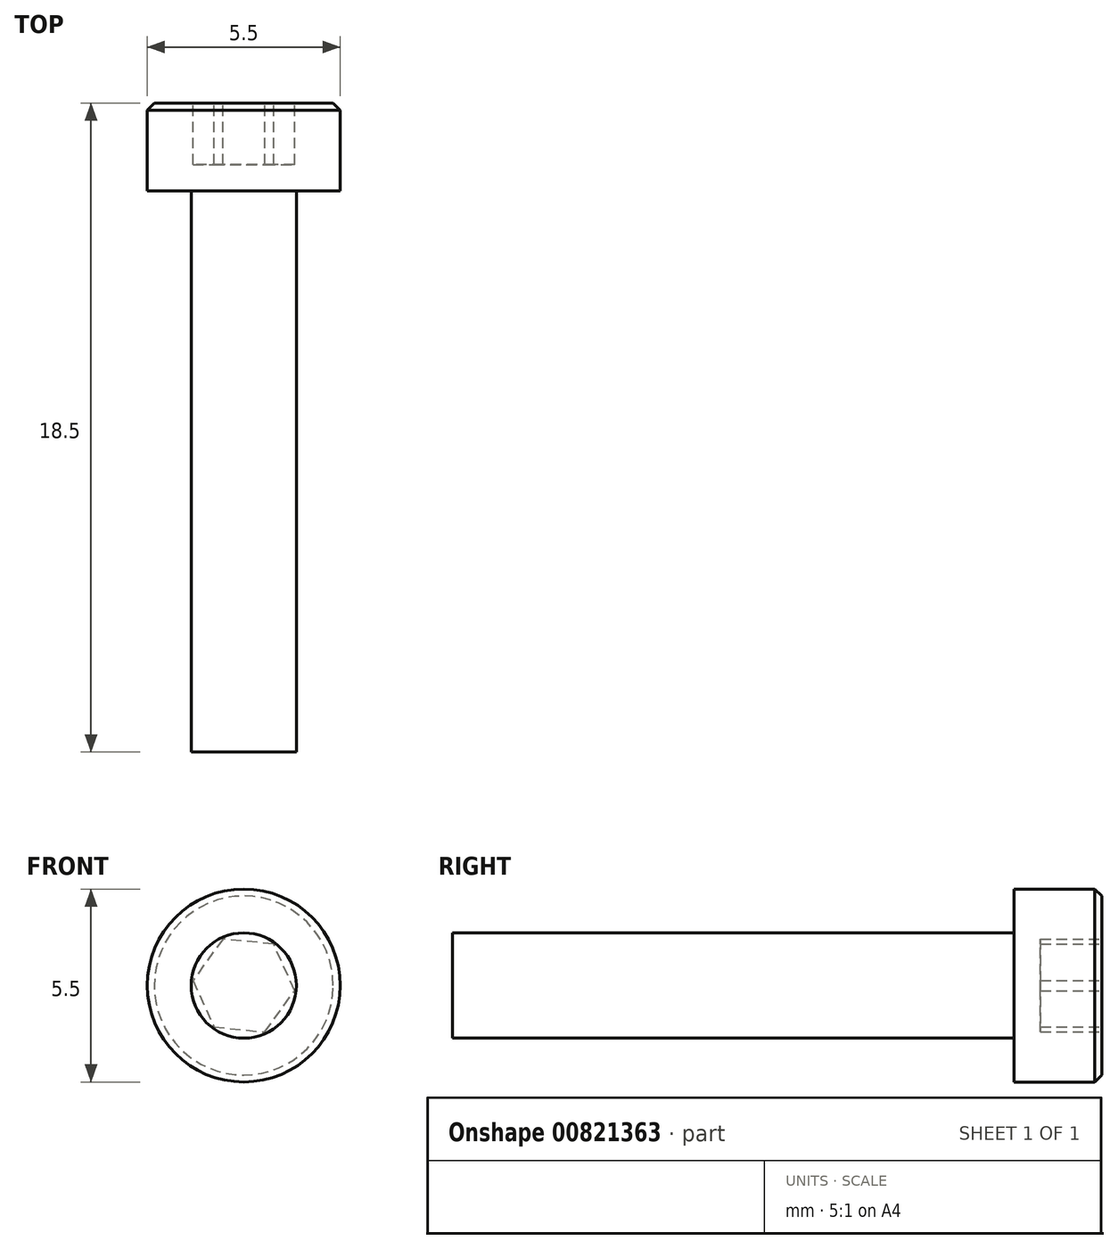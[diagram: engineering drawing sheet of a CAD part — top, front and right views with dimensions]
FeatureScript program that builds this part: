
annotation { "Feature Type Name" : "Feature", "Feature Type Description" : "" }
export const myFeature = defineFeature(function(context is Context, id is Id, definition is map)
    precondition{}
    {
        {
            var Q0;
            Q0=qCreatedBy(makeId("Front.planeOp"),FACE);
            var sketch = newSketch(context, id + "F0", { "sketchPlane" : qUnion([Q0])});
            skCircle(sketch, "E0", {"center": v(0, 0) * mm, "radius": 2.75 * mm});
            skSolve(sketch);
        }
        {
            var Q0;
            Q0=makeQuery(id+"F0.imprint","IMPRINT",FACE,{"disambiguationData":[TD([[makeQuery(id+"F0.imprint","IMPRINT",EDGE,{"derivedFrom":sQuery(id+"F0.wireOp",EDGE,"E0")}),1.0]])]});
            extrude(context, id + "F1", {"entities" : qUnion([Q0]), "depth" : 2.5 * mm, "offsetDistance" : 25 * mm});
        }
        {
            var Q0;
            Q0=makeQuery(id+"F1.opExtrude","CAP_FACE",FACE,{"disambiguationData":[OSD([sQuery(id+"F0.wireOp",EDGE,"E0")])],"isStart":true});
            var sketch = newSketch(context, id + "F2", { "sketchPlane" : qUnion([Q0])});
            skCircle(sketch, "E1.cCircle", {"center": v(0, 0) * mm, "radius": 1.26 * mm, "construction": true});
            skLineSegment(sketch, "E1.0", {"start": v(0.6, 1.33) * mm, "end": v(1.45, 0.15) * mm});
            skLineSegment(sketch, "E1.1", {"start": v(1.45, 0.15) * mm, "end": v(0.85, -1.18) * mm});
            skLineSegment(sketch, "E1.2", {"start": v(0.85, -1.18) * mm, "end": v(-0.6, -1.33) * mm});
            skLineSegment(sketch, "E1.3", {"start": v(-0.6, -1.33) * mm, "end": v(-1.45, -0.15) * mm});
            skLineSegment(sketch, "E1.4", {"start": v(-1.45, -0.15) * mm, "end": v(-0.85, 1.18) * mm});
            skLineSegment(sketch, "E1.5", {"start": v(-0.85, 1.18) * mm, "end": v(0.6, 1.33) * mm});
            skPoint(sketch, "E1.0.midPoint", {"position": v(1.02, 0.74) * mm});
            skSolve(sketch);
        }
        {
            var Q0;
            Q0 = qSketchRegion(id + "F2", true);
            extrude(context, id + "F3", {"entities" : qUnion([Q0]), "operationType" : NewBodyOperationType.REMOVE, "oppositeDirection" : true, "depth" : 1.75 * mm, "offsetDistance" : 25 * mm});
        }
        {
            var Q0;
            Q0=makeQuery(id+"F1.opExtrude","CAP_EDGE",EDGE,{"disambiguationData":[OSD([sQuery(id+"F0.wireOp",EDGE,"E0")])],"isStart":true});
            chamfer(context, id + "F4", {"entities" : qUnion([Q0]), "width" : .2 * mm, "tangentPropagation" : true});
        }
        {
            var Q0;
            Q0=makeQuery(id+"F1.opExtrude","CAP_FACE",FACE,{"disambiguationData":[OSD([sQuery(id+"F0.wireOp",EDGE,"E0")])],"isStart":false});
            var sketch = newSketch(context, id + "F5", { "sketchPlane" : qUnion([Q0])});
            skCircle(sketch, "E2", {"center": v(0, 0) * mm, "radius": 1.5 * mm});
            skSolve(sketch);
        }
        {
            var Q0;
            Q0=makeQuery(id+"F5.imprint","IMPRINT",FACE,{"disambiguationData":[TD([[makeQuery(id+"F5.imprint","IMPRINT",EDGE,{"derivedFrom":sQuery(id+"F5.wireOp",EDGE,"E2")}),1.0]])]});
            extrude(context, id + "F6", {"entities" : qUnion([Q0]), "operationType" : NewBodyOperationType.ADD, "depth" : 16 * mm, "offsetDistance" : 25 * mm});
        }
    });
